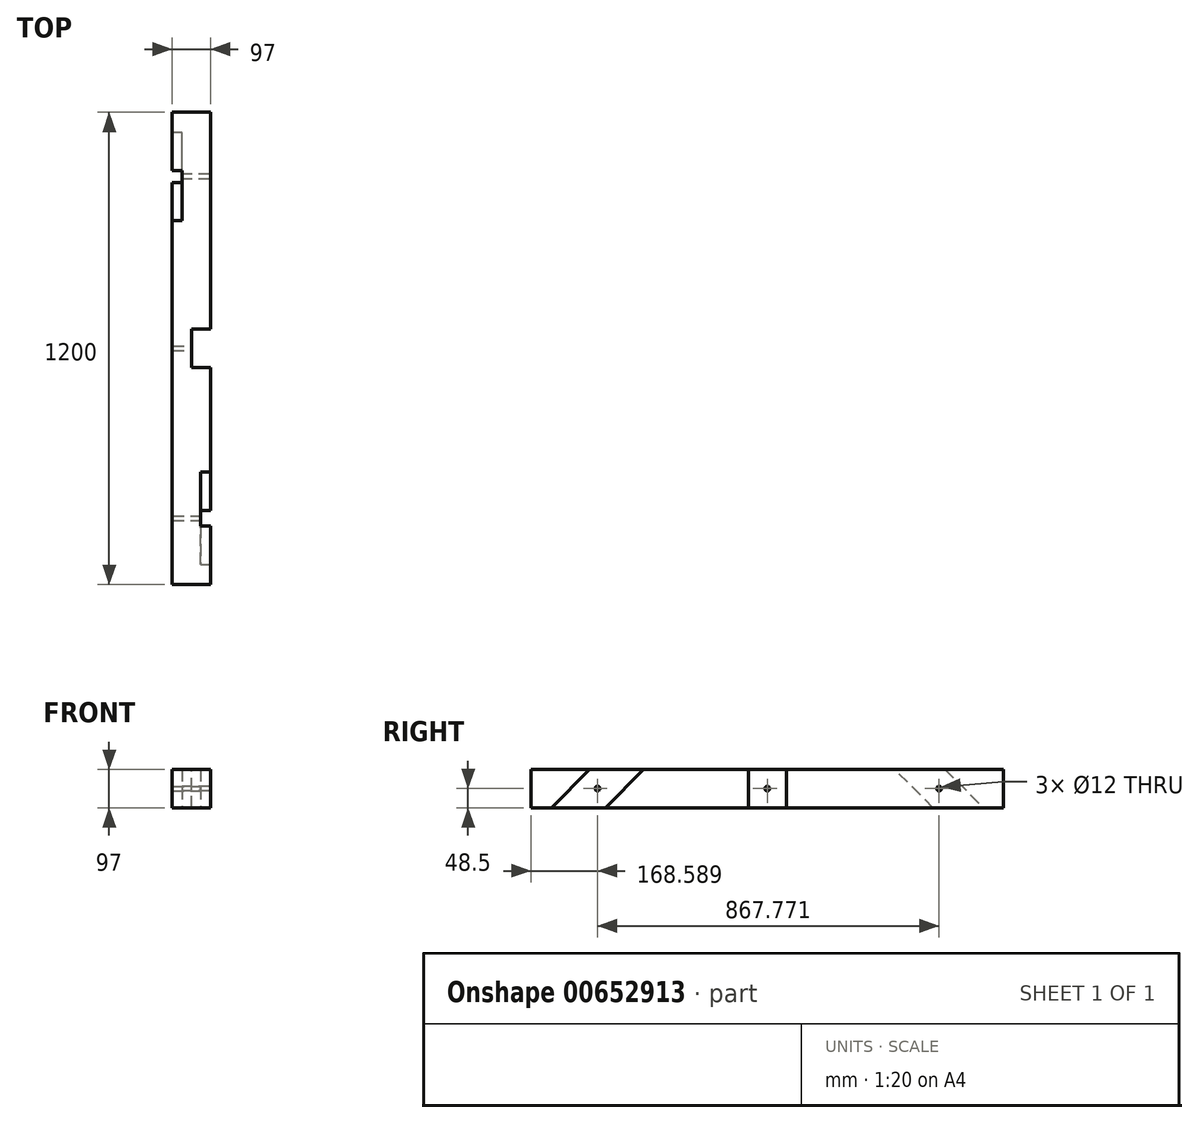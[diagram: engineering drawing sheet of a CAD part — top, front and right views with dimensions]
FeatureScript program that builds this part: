
annotation { "Feature Type Name" : "Feature", "Feature Type Description" : "" }
export const myFeature = defineFeature(function(context is Context, id is Id, definition is map)
    precondition{}
    {
        {
            var Q0;
            Q0=qCreatedBy(makeId("Front.planeOp"),FACE);
            var sketch = newSketch(context, id + "F0", { "sketchPlane" : qUnion([Q0])});
            skLineSegment(sketch, "E0.bottom", {"start": v(-48.5, -48.5) * mm, "end": v(48.5, -48.5) * mm});
            skLineSegment(sketch, "E0.top", {"start": v(-48.5, 48.5) * mm, "end": v(48.5, 48.5) * mm});
            skLineSegment(sketch, "E0.left", {"start": v(-48.5, -48.5) * mm, "end": v(-48.5, 48.5) * mm});
            skLineSegment(sketch, "E0.right", {"start": v(48.5, -48.5) * mm, "end": v(48.5, 48.5) * mm});
            skPoint(sketch, "E0.middle", {"position": v(0, 0) * mm});
            skSolve(sketch);
        }
        {
            var Q0;
            Q0 = qSketchRegion(id + "F0", true);
            extrude(context, id + "F1", {"entities" : qUnion([Q0]), "endBound" : BoundingType.SYMMETRIC, "depth" : 1200 * mm, "offsetDistance" : 25 * mm});
        }
        {
            var Q0;
            Q0=makeQuery(id+"F1.opExtrude","SWEPT_FACE",FACE,{"disambiguationData":[OSD([sQuery(id+"F0.wireOp",EDGE,"E0.right")])]});
            var sketch = newSketch(context, id + "F2", { "sketchPlane" : qUnion([Q0])});
            skLineSegment(sketch, "E1.bottom", {"start": v(-48.5, -48.5) * mm, "end": v(48.5, -48.5) * mm});
            skLineSegment(sketch, "E1.top", {"start": v(-48.5, 48.5) * mm, "end": v(48.5, 48.5) * mm});
            skLineSegment(sketch, "E1.left", {"start": v(-48.5, -48.5) * mm, "end": v(-48.5, 48.5) * mm});
            skLineSegment(sketch, "E1.right", {"start": v(48.5, -48.5) * mm, "end": v(48.5, 48.5) * mm});
            skPoint(sketch, "E1.middle", {"position": v(0, 0) * mm});
            skSolve(sketch);
        }
        {
            var Q0;
            Q0 = qSketchRegion(id + "F2", true);
            extrude(context, id + "F3", {"entities" : qUnion([Q0]), "operationType" : NewBodyOperationType.REMOVE, "oppositeDirection" : true, "depth" : (97 / 2) * mm, "offsetDistance" : 25 * mm});
        }
        {
            var Q0;
            {var subQ1=sQuery(id+"F0.wireOp",EDGE,"E0.right");Q0=makeQuery(id+"F3.boolean.opBoolean","SPLIT",FACE,{"disambiguationData":[TD([makeQuery(id+"F3.opExtrude","SWEPT_FACE",FACE,{"disambiguationData":[OSD([sQuery(id+"F2.wireOp",EDGE,"E1.left")])]})])],"derivedFrom":makeQuery(id+"F1.opExtrude","SWEPT_FACE",FACE,{"disambiguationData":[OSD([subQ1])]})});}
            var sketch = newSketch(context, id + "F4", { "sketchPlane" : qUnion([Q0])});
            skLineSegment(sketch, "E2", {"start": v(-451.5, 48.5) * mm, "end": v(-548.5, -48.5) * mm});
            skLineSegment(sketch, "E3", {"start": v(-548.5, -48.5) * mm, "end": v(-411.32, -48.5) * mm});
            skLineSegment(sketch, "E4", {"start": v(-411.32, -48.5) * mm, "end": v(-314.32, 48.5) * mm});
            skLineSegment(sketch, "E5", {"start": v(-314.32, 48.5) * mm, "end": v(-451.5, 48.5) * mm});
            skSolve(sketch);
        }
        {
            var Q0;
            Q0 = qSketchRegion(id + "F4", true);
            extrude(context, id + "F5", {"entities" : qUnion([Q0]), "operationType" : NewBodyOperationType.REMOVE, "oppositeDirection" : true, "depth" : 25 * mm, "offsetDistance" : 25 * mm});
        }
        {
            var Q0;
            Q0=makeQuery(id+"F1.opExtrude","SWEPT_FACE",FACE,{"disambiguationData":[OSD([sQuery(id+"F0.wireOp",EDGE,"E0.left")])]});
            var sketch = newSketch(context, id + "F6", { "sketchPlane" : qUnion([Q0])});
            skLineSegment(sketch, "E6", {"start": v(-451.5, 48.5) * mm, "end": v(-548.5, -48.5) * mm});
            skLineSegment(sketch, "E7", {"start": v(-548.5, -48.5) * mm, "end": v(-421.22, -48.5) * mm});
            skLineSegment(sketch, "E8", {"start": v(-421.22, -48.5) * mm, "end": v(-324.22, 48.5) * mm});
            skLineSegment(sketch, "E9", {"start": v(-324.22, 48.5) * mm, "end": v(-451.5, 48.5) * mm});
            skSolve(sketch);
        }
        {
            var Q0;
            Q0 = qSketchRegion(id + "F6", true);
            extrude(context, id + "F7", {"entities" : qUnion([Q0]), "operationType" : NewBodyOperationType.REMOVE, "oppositeDirection" : true, "depth" : 25 * mm, "offsetDistance" : 25 * mm});
        }
        {
            var Q0;
            Q0=makeQuery(id+"F5.boolean.opBoolean","COPY",FACE,{"derivedFrom":makeQuery(id+"F5.opExtrude","CAP_FACE",FACE,{"disambiguationData":[OSD([sQuery(id+"F4.wireOp",EDGE,"E2"),sQuery(id+"F4.wireOp",EDGE,"E3"),sQuery(id+"F4.wireOp",EDGE,"E4"),sQuery(id+"F4.wireOp",EDGE,"E5")])],"isStart":false})});
            var sketch = newSketch(context, id + "F8", { "sketchPlane" : qUnion([Q0])});
            skLineSegment(sketch, "E10", {"start": v(-500, 0) * mm, "end": v(-431.41, 0) * mm, "construction": true});
            skLineSegment(sketch, "E11", {"start": v(-431.41, 0) * mm, "end": v(-362.82, 0) * mm, "construction": true});
            skCircle(sketch, "E12", {"center": v(-431.41, 0) * mm, "radius": 6 * mm});
            skSolve(sketch);
        }
        {
            var Q0;
            Q0 = qSketchRegion(id + "F8", true);
            extrude(context, id + "F9", {"entities" : qUnion([Q0]), "operationType" : NewBodyOperationType.REMOVE, "endBound" : BoundingType.UP_TO_NEXT, "oppositeDirection" : true, "depth" : 25 * mm, "offsetDistance" : 25 * mm});
        }
        {
            var Q0;
            Q0=makeQuery(id+"F3.boolean.opBoolean","COPY",FACE,{"derivedFrom":makeQuery(id+"F3.opExtrude","CAP_FACE",FACE,{"disambiguationData":[OSD([sQuery(id+"F2.wireOp",EDGE,"E1.bottom"),sQuery(id+"F2.wireOp",EDGE,"E1.top"),sQuery(id+"F2.wireOp",EDGE,"E1.left"),sQuery(id+"F2.wireOp",EDGE,"E1.right")])],"isStart":false})});
            var sketch = newSketch(context, id + "F10", { "sketchPlane" : qUnion([Q0])});
            skCircle(sketch, "E13", {"center": v(0, 0) * mm, "radius": 6 * mm});
            skSolve(sketch);
        }
        {
            var Q0;
            Q0 = qSketchRegion(id + "F10", true);
            extrude(context, id + "F11", {"entities" : qUnion([Q0]), "operationType" : NewBodyOperationType.REMOVE, "endBound" : BoundingType.UP_TO_NEXT, "oppositeDirection" : true, "depth" : 25 * mm, "offsetDistance" : 25 * mm});
        }
        {
            var Q0;
            Q0=makeQuery(id+"F7.boolean.opBoolean","COPY",FACE,{"derivedFrom":makeQuery(id+"F7.opExtrude","CAP_FACE",FACE,{"disambiguationData":[OSD([sQuery(id+"F6.wireOp",EDGE,"E6"),sQuery(id+"F6.wireOp",EDGE,"E7"),sQuery(id+"F6.wireOp",EDGE,"E8"),sQuery(id+"F6.wireOp",EDGE,"E9")])],"isStart":false})});
            var sketch = newSketch(context, id + "F12", { "sketchPlane" : qUnion([Q0])});
            skLineSegment(sketch, "E14", {"start": v(-500, 0) * mm, "end": v(-372.72, 0) * mm, "construction": true});
            skCircle(sketch, "E15", {"center": v(-436.36, 0) * mm, "radius": 6 * mm});
            skSolve(sketch);
        }
        {
            var Q0;
            Q0 = qSketchRegion(id + "F12", true);
            extrude(context, id + "F13", {"entities" : qUnion([Q0]), "operationType" : NewBodyOperationType.REMOVE, "endBound" : BoundingType.UP_TO_NEXT, "oppositeDirection" : true, "depth" : 25 * mm, "offsetDistance" : 25 * mm});
        }
    });
